# Revit family: Boomerrain Ø 315
name_source: partatom
category: Air Terminals
units: mm (PartAtom-declared; Revit-internal decimal feet)

## family parameters
Always vertical = No
Cut with Voids When Loaded = Yes
Part Type = Normal
Room Calculation Point = No
Round Connector Dimension = Use Diameter
Shared = No
Work Plane-Based = No

## types (1)
- Boomerrain Ø 315
    Description = With its special geometry and aerodynamic design, Boomerain® - Airmaster’s own range of façade ventilation grills – has some truly unique properties. Boomerain is therefore “patent pending”.

The shape of the slats has been designed in such a way that only very limited turbulence occurs on the reverse of the façade ventilation grill. Pressure loss is thus reduced, and energy consumption is reduced considerably. The unique geometry is furthermore designed to capture water droplets and channel them away, preventing penetration into the duct.

Boomerain’s aerodynamic design means that it is now possible to reduce the diameter of the duct connection on several Airmaster ventilation units, and thus the diameter of the hole in the façade, without additional pressure loss and entrainment of rainwater.

Boomerain dimensions:

Ø160 – fits Airmaster AM 300
Ø250 – fits Airmaster AM 500
Ø315 – fits Airmaster AM 800, AM 900, AM 1000, AM 1200 and DV 1000
We install Airmaster ventilation units in vastly different geographical conditions in Europe – from a mild inland climate to the harsh west coast climate in Norway, for example.
Different weather conditions pose different challenges for a façade ventilation grill. We’ve addressed this by producing three different versions.
    Manufacturer = Airmaster A/S
    Model = BOOMERAIN®
    Publication date = 09.08.2023
    URL = https://www.airmaster-as.com
    Version number = 1.2

## geometry (parser evidence)
native form markers: Sweep x2
no freeform markers — native parametric forms only
